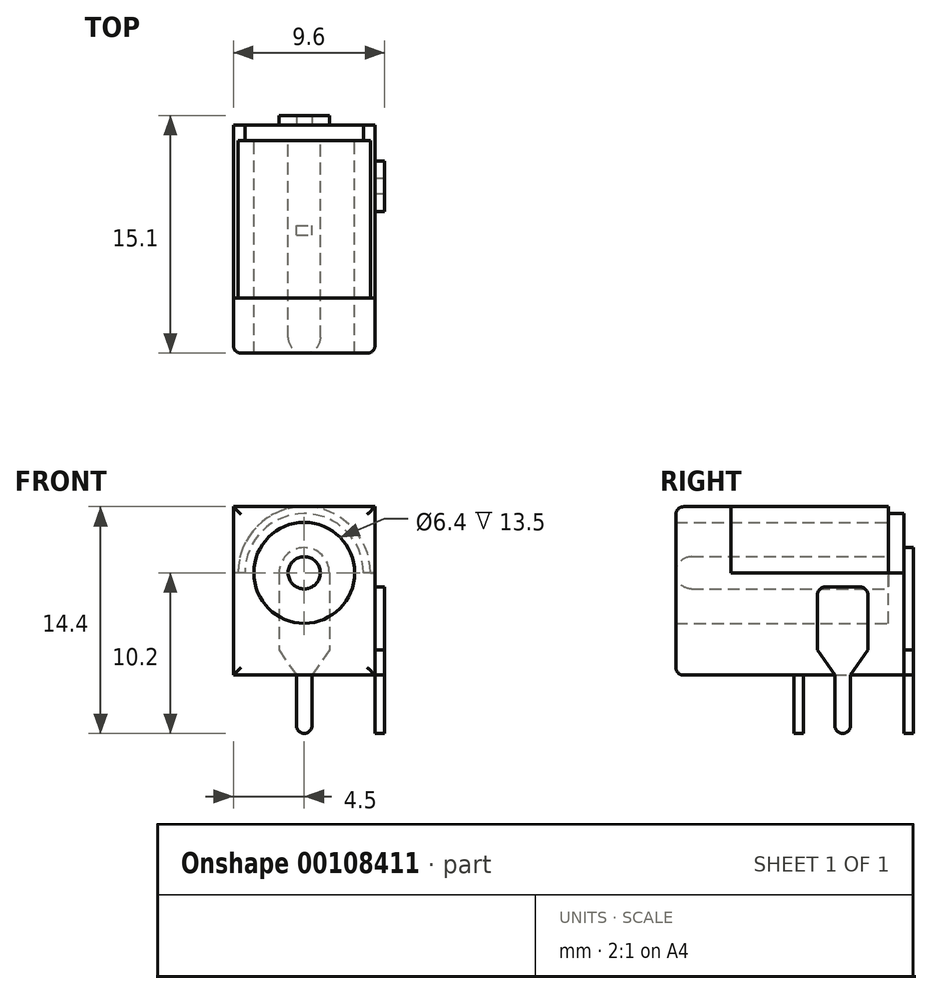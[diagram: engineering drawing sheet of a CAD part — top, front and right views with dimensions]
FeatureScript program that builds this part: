
annotation { "Feature Type Name" : "Feature", "Feature Type Description" : "" }
export const myFeature = defineFeature(function(context is Context, id is Id, definition is map)
    precondition{}
    {
        {
            var Q0;
            Q0=qCreatedBy(makeId("Front.planeOp"),FACE);
            var sketch = newSketch(context, id + "F0", { "sketchPlane" : qUnion([Q0])});
            skLineSegment(sketch, "E0", {"start": v(0, 0) * mm, "end": v(0, 4.2) * mm, "construction": true});
            skLineSegment(sketch, "E1", {"start": v(0, 0) * mm, "end": v(-4.5, 0) * mm});
            skLineSegment(sketch, "E2.bottom", {"start": v(-4.5, 4.2) * mm, "end": v(4.5, 4.2) * mm});
            skLineSegment(sketch, "E2.top", {"start": v(-4.5, -6.5) * mm, "end": v(4.5, -6.5) * mm});
            skLineSegment(sketch, "E2.left", {"start": v(-4.5, 4.2) * mm, "end": v(-4.5, -6.5) * mm});
            skLineSegment(sketch, "E2.right", {"start": v(4.5, 4.2) * mm, "end": v(4.5, -6.5) * mm});
            skLineSegment(sketch, "E3", {"start": v(0, 0) * mm, "end": v(0, -6.5) * mm, "construction": true});
            skLineSegment(sketch, "E4", {"start": v(0, 0) * mm, "end": v(4.5, 0) * mm});
            skCircle(sketch, "E5", {"center": v(0, 0) * mm, "radius": 3.2 * mm});
            skCircle(sketch, "E6", {"center": v(0, 0) * mm, "radius": 1 * mm});
            skCircle(sketch, "E7", {"center": v(0, 0) * mm, "radius": 4.2 * mm});
            skSolve(sketch);
        }
        {
            var Q0;
            Q0=makeQuery(id+"F0.imprint","IMPRINT",FACE,{"disambiguationData":[TD([[makeQuery(id+"F0.imprint","IMPRINT",EDGE,{"derivedFrom":sQuery(id+"F0.wireOp",EDGE,"E5")}),-1.0]])]});
            var Q1;
            Q1=makeQuery(id+"F0.imprint","IMPRINT",FACE,{"disambiguationData":[TD([[makeQuery(id+"F0.imprint","IMPRINT",EDGE,{"derivedFrom":sQuery(id+"F0.wireOp",EDGE,"E2.top")}),1.0]])]});
            var Q2;
            {var subQ0=sQuery(id+"F0.wireOp",EDGE,"E2.right");var subQ1=sQuery(id+"F0.wireOp",EDGE,"E2.bottom");var subQ2=makeQuery(id+"F0.imprint","INTERSECT",VERTEX,{"derivedFrom":[subQ1,subQ0]});Q2=makeQuery(id+"F0.imprint","IMPRINT",FACE,{"disambiguationData":[TD([[makeQuery(id+"F0.imprint","IMPRINT",EDGE,{"disambiguationData":[TD([[subQ2,1.0]])],"derivedFrom":subQ1}),-1.0]])]});}
            var Q3;
            {var subQ4=sQuery(id+"F0.wireOp",EDGE,"E5");var subQ5=sQuery(id+"F0.wireOp",EDGE,"E1");var subQ6=makeQuery(id+"F0.imprint","INTERSECT",VERTEX,{"derivedFrom":[subQ5,subQ4]});Q3=makeQuery(id+"F0.imprint","IMPRINT",FACE,{"disambiguationData":[TD([[makeQuery(id+"F0.imprint","IMPRINT",EDGE,{"disambiguationData":[TD([[subQ6,-1.0]])],"derivedFrom":subQ5}),-1.0]])]});}
            var Q4;
            {var subQ0=sQuery(id+"F0.wireOp",EDGE,"E2.left");var subQ1=sQuery(id+"F0.wireOp",EDGE,"E1");var subQ2=makeQuery(id+"F0.imprint","INTERSECT",VERTEX,{"derivedFrom":[subQ1,subQ0]});Q4=makeQuery(id+"F0.imprint","IMPRINT",FACE,{"disambiguationData":[TD([[makeQuery(id+"F0.imprint","IMPRINT",EDGE,{"disambiguationData":[TD([[subQ2,1.0]])],"derivedFrom":subQ1}),-1.0]])]});}
            extrude(context, id + "F1", {"entities" : qUnion([Q0, Q1, Q2, Q3, Q4]), "depth" : 3.5 * mm});
        }
        {
            var Q0;
            {var subQ4=sQuery(id+"F0.wireOp",EDGE,"E5");var subQ5=sQuery(id+"F0.wireOp",EDGE,"E1");var subQ6=makeQuery(id+"F0.imprint","INTERSECT",VERTEX,{"derivedFrom":[subQ5,subQ4]});Q0=makeQuery(id+"F0.imprint","IMPRINT",FACE,{"disambiguationData":[TD([[makeQuery(id+"F0.imprint","IMPRINT",EDGE,{"disambiguationData":[TD([[subQ6,-1.0]])],"derivedFrom":subQ5}),-1.0]])]});}
            var Q1;
            {var subQ1=sQuery(id+"F0.wireOp",EDGE,"E2.top");Q1=makeQuery(id+"F0.imprint","IMPRINT",FACE,{"disambiguationData":[TD([[makeQuery(id+"F0.imprint","IMPRINT",EDGE,{"derivedFrom":subQ1}),1.0]])]});}
            var Q2;
            {var subQ0=sQuery(id+"F0.wireOp",EDGE,"E5");var subQ1=sQuery(id+"F0.wireOp",EDGE,"E1");var subQ2=makeQuery(id+"F0.imprint","INTERSECT",VERTEX,{"derivedFrom":[subQ1,subQ0]});Q2=makeQuery(id+"F0.imprint","IMPRINT",FACE,{"disambiguationData":[TD([[makeQuery(id+"F0.imprint","IMPRINT",EDGE,{"disambiguationData":[TD([[subQ2,-1.0]])],"derivedFrom":subQ1}),1.0]])]});}
            var Q3;
            Q3=makeQuery(id+"F1.opExtrude","CAP_FACE",FACE,{"disambiguationData":[OSD([sQuery(id+"F0.wireOp",EDGE,"E6")])],"isStart":true});
            extrude(context, id + "F2", {"entities" : qUnion([Q0, Q1, Q2, Q3]), "operationType" : NewBodyOperationType.ADD, "oppositeDirection" : true, "depth" : 10 * mm});
        }
        {
            var Q0;
            Q0=makeQuery(id+"F2.opExtrude","CAP_FACE",FACE,{"disambiguationData":[OSD([sQuery(id+"F0.wireOp",EDGE,"E1"),sQuery(id+"F0.wireOp",EDGE,"E2.top"),sQuery(id+"F0.wireOp",EDGE,"E2.left"),sQuery(id+"F0.wireOp",EDGE,"E2.right"),sQuery(id+"F0.wireOp",EDGE,"E4"),sQuery(id+"F0.wireOp",EDGE,"E5"),sQuery(id+"F0.wireOp",EDGE,"E7")])],"isStart":false});
            var sketch = newSketch(context, id + "F9", { "sketchPlane" : qUnion([Q0])});
            skLineSegment(sketch, "E8.bottom", {"start": v(-4.5, 0) * mm, "end": v(4.5, 0) * mm});
            skLineSegment(sketch, "E8.top", {"start": v(-4.5, -6.5) * mm, "end": v(4.5, -6.5) * mm});
            skLineSegment(sketch, "E8.left", {"start": v(-4.5, 0) * mm, "end": v(-4.5, -6.5) * mm});
            skLineSegment(sketch, "E8.right", {"start": v(4.5, 0) * mm, "end": v(4.5, -6.5) * mm});
            skCircle(sketch, "E9", {"center": v(0, 0) * mm, "radius": 3.76 * mm});
            skSolve(sketch);
        }
        {
            var Q0;
            {var subQ0=sQuery(id+"F9.wireOp",EDGE,"E9");var subQ1=sQuery(id+"F9.wireOp",EDGE,"E8.bottom");var subQ2=makeQuery(id+"F9.imprint","INTERSECT",VERTEX,{"disambiguationData":[OD(0.0)],"derivedFrom":[subQ1,subQ0]});Q0=makeQuery(id+"F9.imprint","IMPRINT",FACE,{"disambiguationData":[TD([[makeQuery(id+"F9.imprint","IMPRINT",EDGE,{"disambiguationData":[TD([[subQ2,-1.0]])],"derivedFrom":subQ1}),1.0]])]});}
            var Q1;
            {var subQ0=sQuery(id+"F9.wireOp",EDGE,"E9");var subQ1=sQuery(id+"F9.wireOp",EDGE,"E8.bottom");var subQ2=makeQuery(id+"F9.imprint","INTERSECT",VERTEX,{"disambiguationData":[OD(0.0)],"derivedFrom":[subQ1,subQ0]});Q1=makeQuery(id+"F9.imprint","IMPRINT",FACE,{"disambiguationData":[TD([[makeQuery(id+"F9.imprint","IMPRINT",EDGE,{"disambiguationData":[TD([[subQ2,-1.0]])],"derivedFrom":subQ1}),-1.0]])]});}
            var Q2;
            Q2=makeQuery(id+"F9.imprint","IMPRINT",FACE,{"disambiguationData":[TD([[makeQuery(id+"F9.imprint","IMPRINT",EDGE,{"derivedFrom":sQuery(id+"F9.wireOp",EDGE,"E8.top")}),-1.0]])]});
            var Q3;
            {var subQ0=sQuery(id+"F9.wireOp",EDGE,"E8.bottom");var subQ1=makeQuery(id+"F2.opExtrude","CAP_EDGE",EDGE,{"disambiguationData":[OSD([sQuery(id+"F0.wireOp",EDGE,"E5")])],"isStart":false});var subQ2=makeQuery(id+"F9.imprint","INTERSECT",VERTEX,{"disambiguationData":[OD(0.0)],"derivedFrom":[subQ1,subQ0]});Q3=makeQuery(id+"F9.imprint","IMPRINT",FACE,{"disambiguationData":[TD([[makeQuery(id+"F9.imprint","IMPRINT",EDGE,{"disambiguationData":[TD([[subQ2,-1.0]])],"derivedFrom":subQ0}),1.0]])]});}
            var Q4;
            {var subQ0=sQuery(id+"F9.wireOp",EDGE,"E8.bottom");var subQ1=makeQuery(id+"F2.opExtrude","CAP_EDGE",EDGE,{"disambiguationData":[OSD([sQuery(id+"F0.wireOp",EDGE,"E5")])],"isStart":false});var subQ2=makeQuery(id+"F9.imprint","INTERSECT",VERTEX,{"disambiguationData":[OD(0.0)],"derivedFrom":[subQ1,subQ0]});Q4=makeQuery(id+"F9.imprint","IMPRINT",FACE,{"disambiguationData":[TD([[makeQuery(id+"F9.imprint","IMPRINT",EDGE,{"disambiguationData":[TD([[subQ2,-1.0]])],"derivedFrom":subQ0}),-1.0]])]});}
            extrude(context, id + "F10", {"entities" : qUnion([Q0, Q1, Q2, Q3, Q4]), "operationType" : NewBodyOperationType.ADD, "depth" : 1 * mm});
        }
        {
            var Q0;
            {var subQ0=sQuery(id+"F0.wireOp",EDGE,"E2.right");Q0=makeQuery(id+"F10.boolean.opBoolean","MERGE",FACE,{"derivedFrom":[makeQuery(id+"F2.boolean.opBoolean","MERGE",FACE,{"derivedFrom":[makeQuery(id+"F1.opExtrude","SWEPT_FACE",FACE,{"disambiguationData":[OSD([subQ0])]}),makeQuery(id+"F2.opExtrude","SWEPT_FACE",FACE,{"disambiguationData":[OSD([subQ0])]})]}),makeQuery(id+"F10.opExtrude","SWEPT_FACE",FACE,{"disambiguationData":[OSD([sQuery(id+"F9.wireOp",EDGE,"E8.left")])]})]});}
            var sketch = newSketch(context, id + "F11", { "sketchPlane" : qUnion([Q0])});
            skLineSegment(sketch, "E10.bottom", {"start": v(-3.5, 4.2) * mm, "end": v(11, 4.2) * mm, "construction": true});
            skLineSegment(sketch, "E10.top", {"start": v(-3.5, -6.5) * mm, "end": v(11, -6.5) * mm, "construction": true});
            skLineSegment(sketch, "E10.left", {"start": v(-3.5, 4.2) * mm, "end": v(-3.5, -6.5) * mm, "construction": true});
            skLineSegment(sketch, "E10.right", {"start": v(11, 4.2) * mm, "end": v(11, -6.5) * mm, "construction": true});
            skLineSegment(sketch, "E11", {"start": v(3.75, 4.2) * mm, "end": v(3.75, -6.5) * mm, "construction": true});
            skLineSegment(sketch, "E12", {"start": v(-3.5, -1.15) * mm, "end": v(11, -1.15) * mm, "construction": true});
            skLineSegment(sketch, "E13", {"start": v(7.1, 4.2) * mm, "end": v(7.1, -6.5) * mm, "construction": true});
            skLineSegment(sketch, "E14.bottom", {"start": v(5.5, -0.9) * mm, "end": v(8.7, -0.9) * mm});
            skLineSegment(sketch, "E14.top", {"start": v(5.5, -4.9) * mm, "end": v(8.7, -4.9) * mm});
            skLineSegment(sketch, "E14.left", {"start": v(5.5, -0.9) * mm, "end": v(5.5, -4.9) * mm});
            skLineSegment(sketch, "E14.right", {"start": v(8.7, -0.9) * mm, "end": v(8.7, -4.9) * mm});
            skLineSegment(sketch, "E15.bottom", {"start": v(6.6, -6.5) * mm, "end": v(7.6, -6.5) * mm});
            skLineSegment(sketch, "E15.top", {"start": v(6.6, -10.2) * mm, "end": v(7.6, -10.2) * mm});
            skLineSegment(sketch, "E15.left", {"start": v(6.6, -6.5) * mm, "end": v(6.6, -10.2) * mm});
            skLineSegment(sketch, "E15.right", {"start": v(7.6, -6.5) * mm, "end": v(7.6, -10.2) * mm});
            skLineSegment(sketch, "E16", {"start": v(5.5, -4.9) * mm, "end": v(6.6, -6.5) * mm});
            skLineSegment(sketch, "E17", {"start": v(8.7, -4.9) * mm, "end": v(7.6, -6.5) * mm});
            skSolve(sketch);
        }
        {
            var Q0;
            Q0=makeQuery(id+"F11.imprint","IMPRINT",FACE,{"disambiguationData":[TD([[makeQuery(id+"F11.imprint","IMPRINT",EDGE,{"derivedFrom":sQuery(id+"F11.wireOp",EDGE,"E15.top")}),1.0]])]});
            var Q1;
            Q1=makeQuery(id+"F11.imprint","IMPRINT",FACE,{"disambiguationData":[TD([[makeQuery(id+"F11.imprint","IMPRINT",EDGE,{"derivedFrom":sQuery(id+"F11.wireOp",EDGE,"E14.top")}),-1.0]])]});
            var Q2;
            Q2=makeQuery(id+"F11.imprint","IMPRINT",FACE,{"disambiguationData":[TD([[makeQuery(id+"F11.imprint","IMPRINT",EDGE,{"derivedFrom":sQuery(id+"F11.wireOp",EDGE,"E14.bottom")}),-1.0]])]});
            extrude(context, id + "F12", {"entities" : qUnion([Q0, Q1, Q2]), "depth" : 0.6 * mm});
        }
        {
            var Q0;
            {var subQ0=sQuery(id+"F0.wireOp",EDGE,"E2.top");Q0=makeQuery(id+"F10.boolean.opBoolean","MERGE",FACE,{"derivedFrom":[makeQuery(id+"F2.boolean.opBoolean","MERGE",FACE,{"derivedFrom":[makeQuery(id+"F1.opExtrude","SWEPT_FACE",FACE,{"disambiguationData":[OSD([subQ0])]}),makeQuery(id+"F2.opExtrude","SWEPT_FACE",FACE,{"disambiguationData":[OSD([subQ0])]})]}),makeQuery(id+"F10.opExtrude","SWEPT_FACE",FACE,{"disambiguationData":[OSD([sQuery(id+"F9.wireOp",EDGE,"E8.top")])]})]});}
            var sketch = newSketch(context, id + "F13", { "sketchPlane" : qUnion([Q0])});
            skLineSegment(sketch, "E18.bottom", {"start": v(-4.5, 3.5) * mm, "end": v(4.5, 3.5) * mm, "construction": true});
            skLineSegment(sketch, "E18.top", {"start": v(-4.5, -11) * mm, "end": v(4.5, -11) * mm, "construction": true});
            skLineSegment(sketch, "E18.left", {"start": v(-4.5, 3.5) * mm, "end": v(-4.5, -11) * mm, "construction": true});
            skLineSegment(sketch, "E18.right", {"start": v(4.5, 3.5) * mm, "end": v(4.5, -11) * mm, "construction": true});
            skLineSegment(sketch, "E19", {"start": v(0, 3.5) * mm, "end": v(0, -11) * mm, "construction": true});
            skLineSegment(sketch, "E20", {"start": v(-4.5, -3.75) * mm, "end": v(4.5, -3.75) * mm, "construction": true});
            skLineSegment(sketch, "E21.bottom", {"start": v(-0.5, -4) * mm, "end": v(0.5, -4) * mm});
            skLineSegment(sketch, "E21.top", {"start": v(-0.5, -4.6) * mm, "end": v(0.5, -4.6) * mm});
            skLineSegment(sketch, "E21.left", {"start": v(-0.5, -4) * mm, "end": v(-0.5, -4.6) * mm});
            skLineSegment(sketch, "E21.right", {"start": v(0.5, -4) * mm, "end": v(0.5, -4.6) * mm});
            skLineSegment(sketch, "E22", {"start": v(-0.5, -4.3) * mm, "end": v(0.5, -4.3) * mm, "construction": true});
            skSolve(sketch);
        }
        {
            var Q0;
            Q0=makeQuery(id+"F13.imprint","IMPRINT",FACE,{"disambiguationData":[TD([[makeQuery(id+"F13.imprint","IMPRINT",EDGE,{"derivedFrom":sQuery(id+"F13.wireOp",EDGE,"E21.bottom")}),-1.0]])]});
            extrude(context, id + "F14", {"entities" : qUnion([Q0]), "depth" : 3.7 * mm});
        }
        {
            var Q0;
            Q0=makeQuery(id+"F10.opExtrude","CAP_FACE",FACE,{"disambiguationData":[OSD([sQuery(id+"F9.wireOp",EDGE,"E8.bottom"),sQuery(id+"F9.wireOp",EDGE,"E8.top"),sQuery(id+"F9.wireOp",EDGE,"E8.left"),sQuery(id+"F9.wireOp",EDGE,"E8.right"),sQuery(id+"F9.wireOp",EDGE,"E9")])],"isStart":false});
            var sketch = newSketch(context, id + "F3", { "sketchPlane" : qUnion([Q0])});
            skCircle(sketch, "E23", {"center": v(0, 0) * mm, "radius": 3.76 * mm, "construction": true});
            skLineSegment(sketch, "E24.bottom", {"start": v(-4.5, 0) * mm, "end": v(4.5, 0) * mm, "construction": true});
            skLineSegment(sketch, "E24.top", {"start": v(-4.5, -6.5) * mm, "end": v(4.5, -6.5) * mm, "construction": true});
            skLineSegment(sketch, "E24.left", {"start": v(-4.5, 0) * mm, "end": v(-4.5, -6.5) * mm, "construction": true});
            skLineSegment(sketch, "E24.right", {"start": v(4.5, 0) * mm, "end": v(4.5, -6.5) * mm, "construction": true});
            skLineSegment(sketch, "E25", {"start": v(0, 3.76) * mm, "end": v(0, -6.5) * mm, "construction": true});
            skCircle(sketch, "E26", {"center": v(0, 0) * mm, "radius": 1.6 * mm});
            skLineSegment(sketch, "E27.bottom", {"start": v(-1.6, 0) * mm, "end": v(1.6, 0) * mm});
            skLineSegment(sketch, "E27.top", {"start": v(-1.6, -4.9) * mm, "end": v(1.6, -4.9) * mm});
            skLineSegment(sketch, "E27.left", {"start": v(-1.6, 0) * mm, "end": v(-1.6, -4.9) * mm});
            skLineSegment(sketch, "E27.right", {"start": v(1.6, 0) * mm, "end": v(1.6, -4.9) * mm});
            skLineSegment(sketch, "E28.bottom", {"start": v(-0.5, -6.5) * mm, "end": v(0.5, -6.5) * mm});
            skLineSegment(sketch, "E28.top", {"start": v(-0.5, -10.2) * mm, "end": v(0.5, -10.2) * mm});
            skLineSegment(sketch, "E28.left", {"start": v(-0.5, -6.5) * mm, "end": v(-0.5, -10.2) * mm});
            skLineSegment(sketch, "E28.right", {"start": v(0.5, -6.5) * mm, "end": v(0.5, -10.2) * mm});
            skLineSegment(sketch, "E29", {"start": v(-1.6, -4.9) * mm, "end": v(-0.5, -6.5) * mm});
            skLineSegment(sketch, "E30", {"start": v(1.6, -4.9) * mm, "end": v(0.5, -6.5) * mm});
            skSolve(sketch);
        }
        {
            var Q0;
            {var subQ0=sQuery(id+"F3.wireOp",EDGE,"E27.bottom");Q0=makeQuery(id+"F3.imprint","IMPRINT",FACE,{"disambiguationData":[TD([[makeQuery(id+"F3.imprint","IMPRINT",EDGE,{"derivedFrom":subQ0}),1.0]])]});}
            var Q1;
            {var subQ0=sQuery(id+"F3.wireOp",EDGE,"E27.bottom");Q1=makeQuery(id+"F3.imprint","IMPRINT",FACE,{"disambiguationData":[TD([[makeQuery(id+"F3.imprint","IMPRINT",EDGE,{"derivedFrom":subQ0}),-1.0]])]});}
            var Q2;
            Q2=makeQuery(id+"F3.imprint","IMPRINT",FACE,{"disambiguationData":[TD([[makeQuery(id+"F3.imprint","IMPRINT",EDGE,{"derivedFrom":sQuery(id+"F3.wireOp",EDGE,"E27.top")}),1.0]])]});
            var Q3;
            Q3=makeQuery(id+"F3.imprint","IMPRINT",FACE,{"disambiguationData":[TD([[makeQuery(id+"F3.imprint","IMPRINT",EDGE,{"derivedFrom":sQuery(id+"F3.wireOp",EDGE,"E27.top")}),-1.0]])]});
            var Q4;
            Q4=makeQuery(id+"F3.imprint","IMPRINT",FACE,{"disambiguationData":[TD([[makeQuery(id+"F3.imprint","IMPRINT",EDGE,{"derivedFrom":sQuery(id+"F3.wireOp",EDGE,"E28.bottom")}),1.0]])]});
            extrude(context, id + "F4", {"entities" : qUnion([Q0, Q1, Q2, Q3, Q4]), "depth" : 0.6 * mm});
        }
        {
            var Q0;
            Q0=makeQuery(id+"F10.opExtrude","CAP_FACE",FACE,{"disambiguationData":[OSD([sQuery(id+"F9.wireOp",EDGE,"E8.bottom"),sQuery(id+"F9.wireOp",EDGE,"E8.top"),sQuery(id+"F9.wireOp",EDGE,"E8.left"),sQuery(id+"F9.wireOp",EDGE,"E8.right"),sQuery(id+"F9.wireOp",EDGE,"E9")])],"isStart":true});
            var sketch = newSketch(context, id + "F5", { "sketchPlane" : qUnion([Q0])});
            skCircle(sketch, "E31", {"center": v(0, 0) * mm, "radius": 1.02 * mm});
            skSolve(sketch);
        }
        {
            var Q0;
            Q0=makeQuery(id+"F5.imprint","IMPRINT",FACE,{"disambiguationData":[TD([[makeQuery(id+"F5.imprint","IMPRINT",EDGE,{"derivedFrom":sQuery(id+"F5.wireOp",EDGE,"E31")}),1.0]])]});
            extrude(context, id + "F6", {"entities" : qUnion([Q0]), "operationType" : NewBodyOperationType.ADD, "depth" : 13.5 * mm});
        }
        {
            var Q0;
            Q0=makeQuery(id+"F1.opExtrude","CAP_EDGE",EDGE,{"disambiguationData":[OSD([sQuery(id+"F0.wireOp",EDGE,"E2.right")])],"isStart":false});
            var Q1;
            Q1=makeQuery(id+"F1.opExtrude","CAP_EDGE",EDGE,{"disambiguationData":[OSD([sQuery(id+"F0.wireOp",EDGE,"E2.bottom")])],"isStart":false});
            var Q2;
            Q2=makeQuery(id+"F1.opExtrude","CAP_EDGE",EDGE,{"disambiguationData":[OSD([sQuery(id+"F0.wireOp",EDGE,"E2.left")])],"isStart":false});
            var Q3;
            Q3=makeQuery(id+"F1.opExtrude","CAP_EDGE",EDGE,{"disambiguationData":[OSD([sQuery(id+"F0.wireOp",EDGE,"E2.top")])],"isStart":false});
            var Q4;
            Q4=makeQuery(id+"F12.opExtrude","SWEPT_EDGE",EDGE,{"disambiguationData":[OSD([sQuery(id+"F11.wireOp",EDGE,"E14.bottom"),sQuery(id+"F11.wireOp",EDGE,"E14.left")])]});
            var Q5;
            Q5=makeQuery(id+"F12.opExtrude","SWEPT_EDGE",EDGE,{"disambiguationData":[OSD([sQuery(id+"F11.wireOp",EDGE,"E14.bottom"),sQuery(id+"F11.wireOp",EDGE,"E14.right")])]});
            var Q6;
            Q6=makeQuery(id+"F12.opExtrude","SWEPT_EDGE",EDGE,{"disambiguationData":[OSD([sQuery(id+"F11.wireOp",EDGE,"E15.top"),sQuery(id+"F11.wireOp",EDGE,"E15.right")])]});
            var Q7;
            Q7=makeQuery(id+"F12.opExtrude","SWEPT_EDGE",EDGE,{"disambiguationData":[OSD([sQuery(id+"F11.wireOp",EDGE,"E15.top"),sQuery(id+"F11.wireOp",EDGE,"E15.left")])]});
            var Q8;
            Q8=makeQuery(id+"F4.opExtrude","SWEPT_EDGE",EDGE,{"disambiguationData":[OSD([sQuery(id+"F3.wireOp",EDGE,"E28.top"),sQuery(id+"F3.wireOp",EDGE,"E28.left")])]});
            var Q9;
            Q9=makeQuery(id+"F4.opExtrude","SWEPT_EDGE",EDGE,{"disambiguationData":[OSD([sQuery(id+"F3.wireOp",EDGE,"E28.top"),sQuery(id+"F3.wireOp",EDGE,"E28.right")])]});
            var Q10;
            Q10=makeQuery(id+"F14.opExtrude","CAP_EDGE",EDGE,{"disambiguationData":[OSD([sQuery(id+"F13.wireOp",EDGE,"E21.left")])],"isStart":false});
            var Q11;
            Q11=makeQuery(id+"F14.opExtrude","CAP_EDGE",EDGE,{"disambiguationData":[OSD([sQuery(id+"F13.wireOp",EDGE,"E21.right")])],"isStart":false});
            fillet(context, id + "F7", {"entities" : qUnion([Q0, Q1, Q2, Q3, Q4, Q5, Q6, Q7, Q8, Q9, Q10, Q11]), "radius" : 0.5 * mm, "tangentPropagation" : true, "allowEdgeOverflow" : false});
        }
        {
            var Q0;
            Q0=makeQuery(id+"F6.opExtrude","CAP_EDGE",EDGE,{"disambiguationData":[OSD([sQuery(id+"F5.wireOp",EDGE,"E31")])],"isStart":false});
            fillet(context, id + "F8", {"entities" : qUnion([Q0]), "radius" : 1 * mm, "tangentPropagation" : true, "allowEdgeOverflow" : false});
        }
    });
